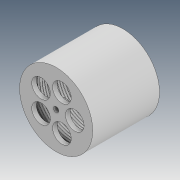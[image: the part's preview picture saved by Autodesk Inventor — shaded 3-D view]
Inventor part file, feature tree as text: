
AUTODESK INVENTOR PART (.ipt)
format: ipt  version: 2020 (Build 240168000, 168)  size: 751,104 bytes
history: native  units: mm
features: sketch x6, extrude x5, helix x1, chamfer x1
ambient origin geometry x8: Origin, YZ Plane, XZ Plane, XY Plane, X Axis, Y Axis, Z Axis, Center Point
bodies: Solid1 (feature_tree)
feature tree (13):
  extrude  "Extrusion1"  Depth=40.0mm
  helix  "Coil1"  [1 undecoded]
  extrude  "Extrusion2"  Depth=1.2mm
  extrude  "Extrusion3"  Depth=10.0mm TaperAngle=0.0deg
  extrude  "Extrusion4"  Depth=12.0mm
  chamfer  "Chamfer1"  Distance=50.0mm Angle=360.0deg
  extrude  "Extrusion5"  Depth=0.6mm
  sketch  "Sketch1"  dims[d0=43.9mm d1=1.6mm d2=40.0mm d3=0.0mm]
  sketch  "Sketch2"  dims[d4=1.2mm d5=0.8mm]
  sketch  "Sketch3"  dims[d6=1.5mm]
  sketch  "Sketch4"  dims[d7=40.0mm d8=10.0mm d9=0.0mm d10=90.0deg d11=90.0deg d12=0.0mm d13=0.0mm d14=20.0mm d15=0.0mm]
  sketch  "Sketch5"  dims[d16=12.0mm d17=12.0mm d18=50.0mm d20=360.0deg]
  sketch  "Sketch6"  dims[d22=3.0mm d23=0.0mm d24=6.6mm d25=4.0mm d26=0.0mm d27=1.0mm d28=2.0mm d29=45.0deg d30=0.6mm d31=0.0mm d32=0.0mm]
note: 1 required parameter value undecoded (feature->parameter linkage not recoverable at this tier; creation-order binding heuristic only, values carry confidence <= 0.55)
